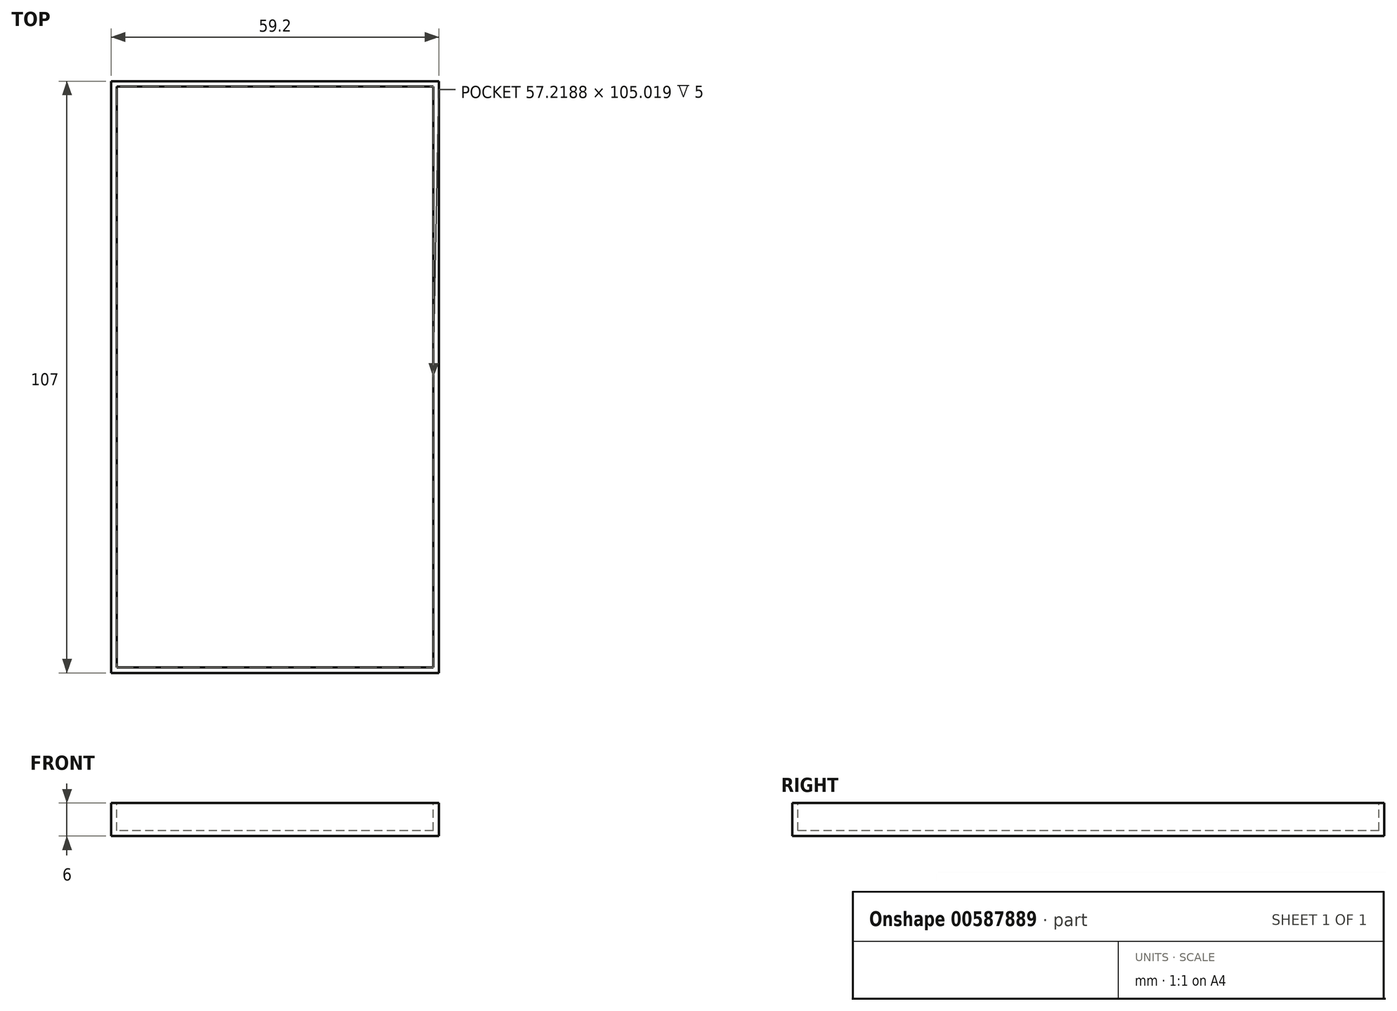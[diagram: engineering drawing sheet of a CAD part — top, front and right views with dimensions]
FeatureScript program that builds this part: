
annotation { "Feature Type Name" : "Feature", "Feature Type Description" : "" }
export const myFeature = defineFeature(function(context is Context, id is Id, definition is map)
    precondition{}
    {
        {
            var Q0;
            Q0=qCreatedBy(makeId("Top.planeOp"),FACE);
            var sketch = newSketch(context, id + "F0", { "sketchPlane" : qUnion([Q0])});
            skLineSegment(sketch, "E0.bottom", {"start": v(-59.2, 52.17) * mm, "end": v(0, 52.17) * mm});
            skLineSegment(sketch, "E0.top", {"start": v(-59.2, -54.83) * mm, "end": v(0, -54.83) * mm});
            skLineSegment(sketch, "E0.left", {"start": v(-59.2, 52.17) * mm, "end": v(-59.2, -54.83) * mm});
            skLineSegment(sketch, "E0.right", {"start": v(0, 52.17) * mm, "end": v(0, -54.83) * mm});
            skSolve(sketch);
        }
        {
            var Q0;
            Q0=makeQuery(id+"F0.imprint","IMPRINT",FACE,{"disambiguationData":[TD([[makeQuery(id+"F0.imprint","IMPRINT",EDGE,{"derivedFrom":sQuery(id+"F0.wireOp",EDGE,"E0.bottom")}),-1.0]])]});
            var Q1;
            Q1 = qSketchRegion(id + "F0", true);
            extrude(context, id + "F1", {"entities" : qUnion([Q0, Q1]), "depth" : 6 * mm, "offsetDistance" : 25.4 * mm});
        }
        {
            var Q0;
            Q0=makeQuery(id+"F1.opExtrude","CAP_FACE",FACE,{"disambiguationData":[OSD([sQuery(id+"F0.wireOp",EDGE,"E0.bottom"),sQuery(id+"F0.wireOp",EDGE,"E0.top"),sQuery(id+"F0.wireOp",EDGE,"E0.left"),sQuery(id+"F0.wireOp",EDGE,"E0.right")])],"isStart":false});
            var sketch = newSketch(context, id + "F2", { "sketchPlane" : qUnion([Q0])});
            skLineSegment(sketch, "E1.bottom", {"start": v(-1, 51.18) * mm, "end": v(-58.2, 51.18) * mm});
            skLineSegment(sketch, "E1.top", {"start": v(-1, -53.84) * mm, "end": v(-58.2, -53.84) * mm});
            skLineSegment(sketch, "E1.left", {"start": v(-1, 51.18) * mm, "end": v(-1, -53.84) * mm});
            skLineSegment(sketch, "E1.right", {"start": v(-58.2, 51.18) * mm, "end": v(-58.2, -53.84) * mm});
            skPoint(sketch, "E1.middle", {"position": v(-29.6, -1.33) * mm});
            skSolve(sketch);
        }
        {
            var Q0;
            Q0=makeQuery(id+"F2.imprint","IMPRINT",FACE,{"disambiguationData":[TD([[makeQuery(id+"F2.imprint","IMPRINT",EDGE,{"derivedFrom":sQuery(id+"F2.wireOp",EDGE,"E1.bottom")}),1.0]])]});
            extrude(context, id + "F3", {"entities" : qUnion([Q0]), "operationType" : NewBodyOperationType.REMOVE, "oppositeDirection" : true, "depth" : 5 * mm, "offsetDistance" : 25.4 * mm});
        }
    });
